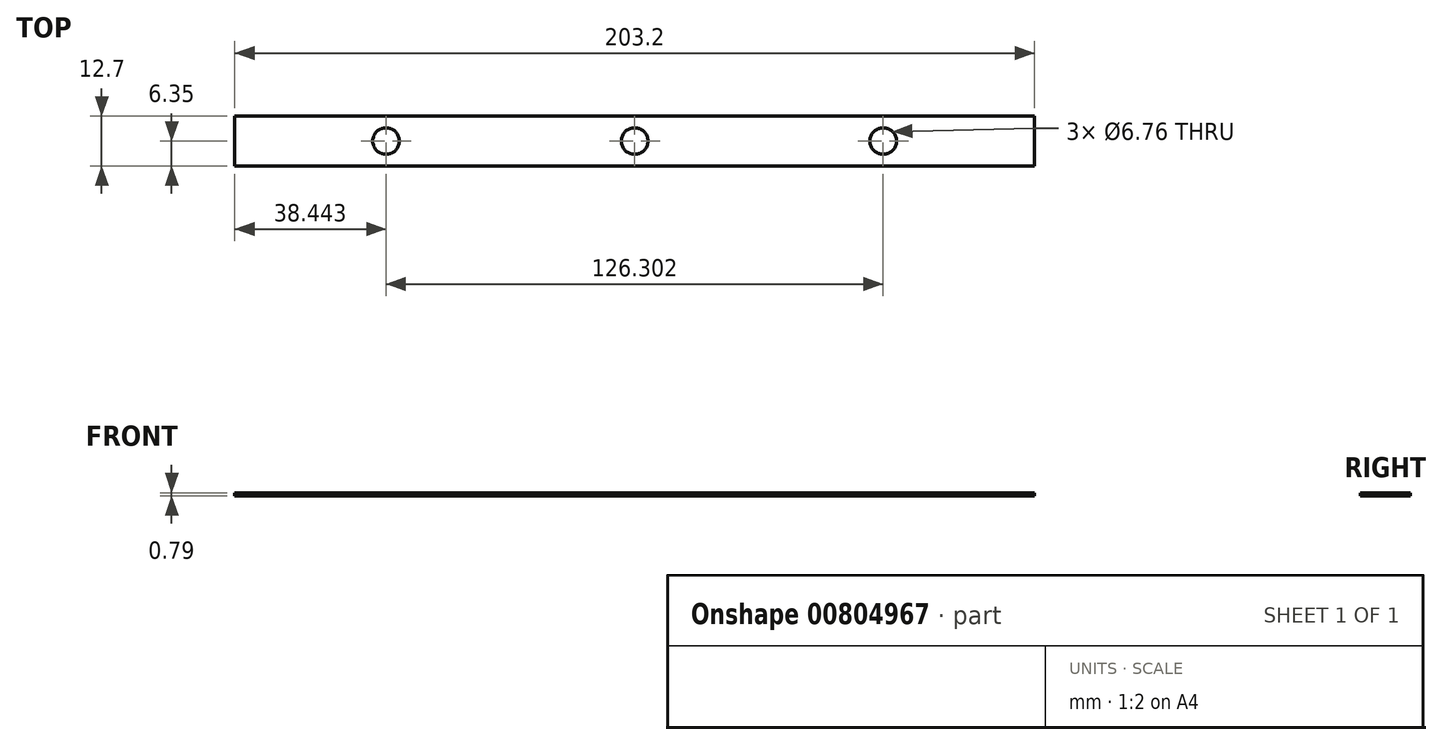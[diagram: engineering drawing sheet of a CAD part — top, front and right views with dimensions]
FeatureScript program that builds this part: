
annotation { "Feature Type Name" : "Feature", "Feature Type Description" : "" }
export const myFeature = defineFeature(function(context is Context, id is Id, definition is map)
    precondition{}
    {
        {
            var Q0;
            Q0=qCreatedBy(makeId("Front.planeOp"),FACE);
            var sketch = newSketch(context, id + "F0", { "sketchPlane" : qUnion([Q0])});
            skLineSegment(sketch, "E0.bottom", {"start": v(0, 0) * mm, "end": v(203.2, 0) * mm});
            skLineSegment(sketch, "E0.top", {"start": v(0, 0.8) * mm, "end": v(203.2, 0.8) * mm});
            skLineSegment(sketch, "E0.left", {"start": v(0, 0) * mm, "end": v(0, 0.8) * mm});
            skLineSegment(sketch, "E0.right", {"start": v(203.2, 0) * mm, "end": v(203.2, 0.8) * mm});
            skArc(sketch, "E1", {"start": v(187.68, 0.8) * mm, "mid": v(101.6, 19.95) * mm, "end": v(15.51, 0.8) * mm});
            skArc(sketch, "E2.0", {"start": v(183.87, 0.8) * mm, "mid": v(101.6, 18.37) * mm, "end": v(19.32, 0.8) * mm});
            skSolve(sketch);
        }
        {
            var Q0;
            Q0=makeQuery(id+"F0.imprint","IMPRINT",FACE,{"disambiguationData":[TD([[makeQuery(id+"F0.imprint","IMPRINT",EDGE,{"derivedFrom":sQuery(id+"F0.wireOp",EDGE,"E0.bottom")}),1.0]])]});
            extrude(context, id + "F1", {"entities" : qUnion([Q0]), "depth" : 12.7 * mm, "offsetDistance" : 25.4 * mm});
        }
        {
            var Q0;
            Q0=makeQuery(id+"F1.opExtrude","SWEPT_FACE",FACE,{"disambiguationData":[OSD([sQuery(id+"F0.wireOp",EDGE,"E0.top")])]});
            var sketch = newSketch(context, id + "F2", { "sketchPlane" : qUnion([Q0])});
            skPoint(sketch, "E3", {"position": v(101.6, -6.35) * mm});
            skPoint(sketch, "E3.positionSnap0", {"position": v(0, -6.35) * mm});
            skPoint(sketch, "E3.positionSnap1", {"position": v(101.6, 0) * mm});
            skPoint(sketch, "E4", {"position": v(38.44, -6.35) * mm});
            skPoint(sketch, "E5", {"position": v(164.74, -6.35) * mm});
            skSolve(sketch);
        }
        {
            var Q0;
            Q0=sQuery(id+"F2.wireOp",VERTEX,"E3");
            var Q1;
            Q1=sQuery(id+"F2.wireOp",VERTEX,"E4");
            var Q2;
            Q2=sQuery(id+"F2.wireOp",VERTEX,"E5");
            var Q3;
            Q3=makeQuery(id+"F1.opExtrude","SWEPT_BODY",BODY,{"disambiguationData":[OSD([sQuery(id+"F0.wireOp",EDGE,"E0.bottom"),sQuery(id+"F0.wireOp",EDGE,"E0.top"),sQuery(id+"F0.wireOp",EDGE,"E0.left"),sQuery(id+"F0.wireOp",EDGE,"E0.right")])]});
            hole(context, id + "F3", {"style" : HoleStyle.SIMPLE, "endStyle" : HoleEndStyle.THROUGH, "standardTappedOrClearance" : lookupTablePath({ "fit" : "Free", "standard" : "ANSI", "size" : "1/4", "type" : "Clearance" }), "standardBlindInLast" : lookupTablePath({ "fit" : "Free", "standard" : "ANSI", "engagement" : "75%", "pitch" : "20 tpi", "size" : "1/4", "type" : "Clearance & tapped" }), "holeDiameter" : 6.76 * mm, "majorDiameter" : 6.35 * mm, "isTappedThrough" : true, "tappedDepth" : 21.17 * mm, "tapClearance" : 3, "startFromSketch" : true, "locations" : qUnion([Q0, Q1, Q2]), "scope" : qUnion([Q3])});
        }
    });
